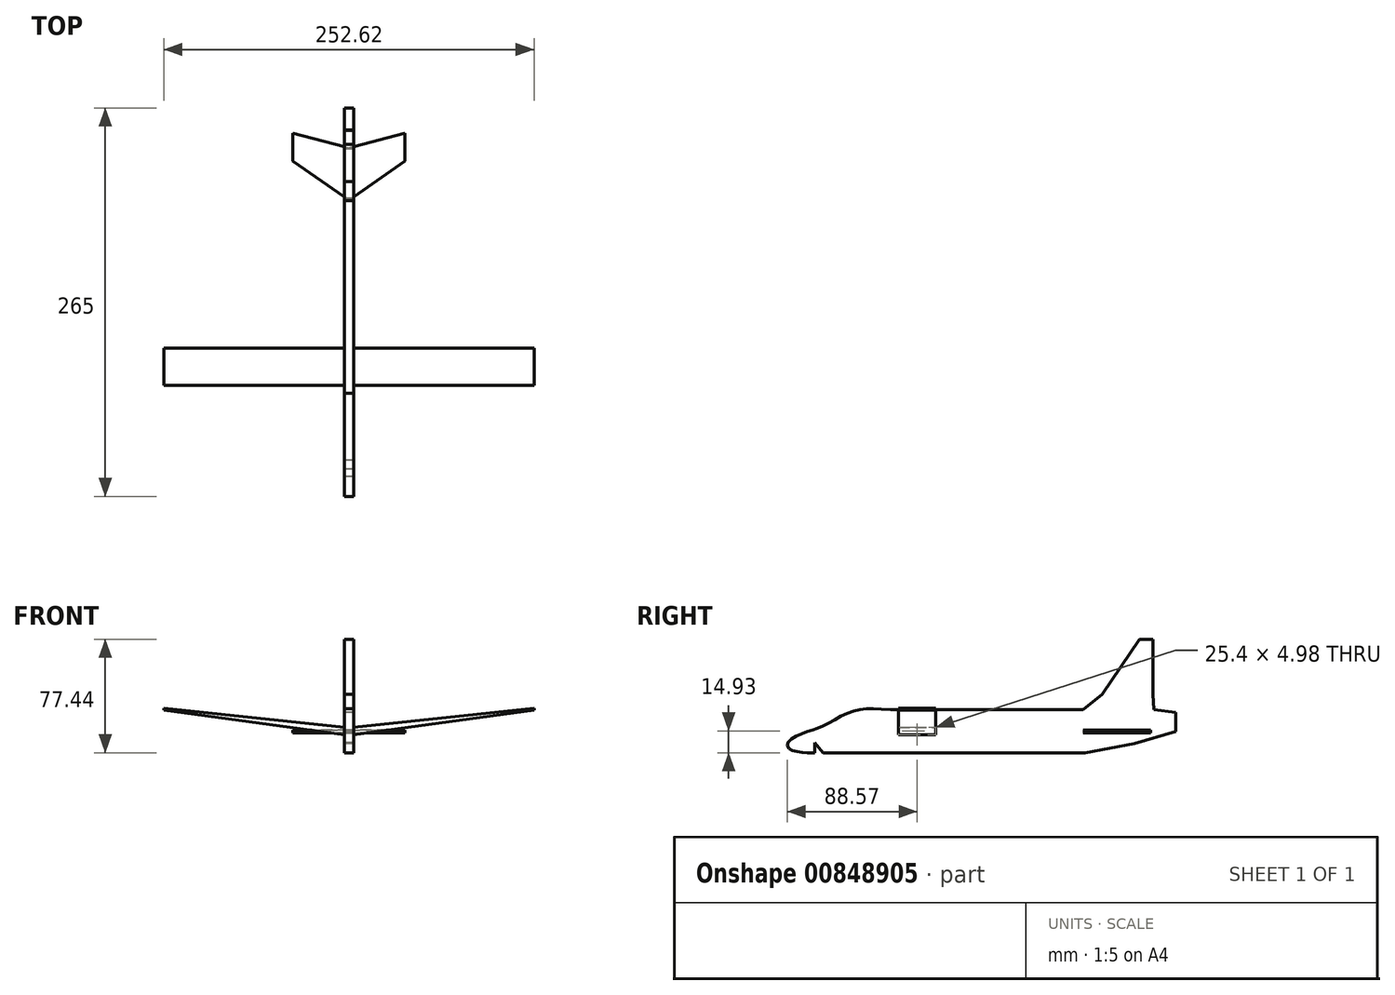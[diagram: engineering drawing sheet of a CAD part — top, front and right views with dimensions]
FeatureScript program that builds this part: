
annotation { "Feature Type Name" : "Feature", "Feature Type Description" : "" }
export const myFeature = defineFeature(function(context is Context, id is Id, definition is map)
    precondition{}
    {
        {
            var Q0;
            Q0=qCreatedBy(makeId("Right.planeOp"),FACE);
            var sketch = newSketch(context, id + "F0", { "sketchPlane" : qUnion([Q0])});
            skLineSegment(sketch, "E0", {"start": v(78.98, -14.55) * mm, "end": v(-51.3, -14.55) * mm});
            skFitSpline(sketch, "E1", {"points": [v(-62.34, -14.55) * mm, v(-73.33, -12.67) * mm, v(-75.7, -8.22) * mm, v(-65.02, -1.1) * mm, v(-51.06, 3.95) * mm, v(-30.97, 13.94) * mm, v(-5.48, 14.83) * mm], "startDerivative": vector(-70.22, 10.78) * mm, "endDerivative": vector(152.13, -6.73) * mm});
            skLineSegment(sketch, "E2", {"start": v(-5.48, 14.83) * mm, "end": v(76.3, 14.83) * mm});
            skLineSegment(sketch, "E3", {"start": v(76.3, 14.83) * mm, "end": v(126.07, 14.83) * mm});
            skLineSegment(sketch, "E4", {"start": v(126.07, 14.83) * mm, "end": v(138.96, 25.3) * mm});
            skLineSegment(sketch, "E5", {"start": v(138.96, 25.3) * mm, "end": v(164.55, 62.89) * mm});
            skLineSegment(sketch, "E6", {"start": v(164.55, 62.89) * mm, "end": v(173.84, 62.89) * mm});
            skLineSegment(sketch, "E7", {"start": v(173.84, 62.89) * mm, "end": v(173.84, 25.3) * mm});
            skLineSegment(sketch, "E8", {"start": v(173.84, 25.3) * mm, "end": v(174.18, 14.83) * mm});
            skPoint(sketch, "E9.startDerivative.orphan", {"position": v(194.66, 0) * mm});
            skLineSegment(sketch, "E10", {"start": v(174.18, 14.83) * mm, "end": v(189.13, 13) * mm});
            skLineSegment(sketch, "E11", {"start": v(189.13, 13) * mm, "end": v(189.13, -0.14) * mm});
            skLineSegment(sketch, "E12", {"start": v(189.13, -0.14) * mm, "end": v(161.15, -8.35) * mm});
            skLineSegment(sketch, "E13", {"start": v(161.15, -8.35) * mm, "end": v(127.42, -14.55) * mm});
            skLineSegment(sketch, "E14", {"start": v(127.42, -14.55) * mm, "end": v(78.98, -14.55) * mm});
            skLineSegment(sketch, "E15", {"start": v(-51.3, -14.55) * mm, "end": v(-57.24, -7.52) * mm});
            skLineSegment(sketch, "E16", {"start": v(-57.24, -14.55) * mm, "end": v(-57.24, -7.52) * mm});
            skLineSegment(sketch, "E17.trimOffspring", {"start": v(-57.24, -14.55) * mm, "end": v(-62.34, -14.55) * mm});
            skSolve(sketch);
        }
        {
            var Q0;
            Q0=qCreatedBy(makeId("Top.planeOp"),FACE);
            var sketch = newSketch(context, id + "F1", { "sketchPlane" : qUnion([Q0])});
            skLineSegment(sketch, "E18", {"start": v(0, 126.19) * mm, "end": v(38.25, 152.85) * mm});
            skLineSegment(sketch, "E19", {"start": v(38.25, 152.85) * mm, "end": v(38.25, 171.97) * mm});
            skLineSegment(sketch, "E20", {"start": v(38.25, 171.97) * mm, "end": v(0, 161.9) * mm});
            skLineSegment(sketch, "E21.MirrorCS", {"start": v(-38.25, 171.97) * mm, "end": v(0, 161.9) * mm});
            skLineSegment(sketch, "E22.MirrorCS", {"start": v(-38.25, 152.85) * mm, "end": v(-38.25, 171.97) * mm});
            skLineSegment(sketch, "E23.MirrorCS", {"start": v(0, 126.19) * mm, "end": v(-38.25, 152.85) * mm});
            skSolve(sketch);
        }
        {
            var Q0;
            Q0 = qSketchRegion(id + "F1", true);
            extrude(context, id + "F2", {"entities" : qUnion([Q0]), "endBound" : BoundingType.SYMMETRIC, "depth" : 1.78 * mm, "offsetDistance" : 25.4 * mm});
        }
        {
            var Q0;
            Q0 = qSketchRegion(id + "F0", true);
            extrude(context, id + "F3", {"entities" : qUnion([Q0]), "endBound" : BoundingType.SYMMETRIC, "depth" : 6.35 * mm, "offsetDistance" : 25.4 * mm});
        }
        {
            var Q0;
            Q0=qCreatedBy(makeId("Front.planeOp"),FACE);
            var sketch = newSketch(context, id + "F4", { "sketchPlane" : qUnion([Q0])});
            skLineSegment(sketch, "E24.0", {"start": v(-126.31, 15.76) * mm, "end": v(-126.31, 14.49) * mm});
            skLineSegment(sketch, "E25", {"start": v(0, 2.54) * mm, "end": v(0, -2.54) * mm});
            skLineSegment(sketch, "E26", {"start": v(-126.31, 15.76) * mm, "end": v(0, 2.54) * mm});
            skLineSegment(sketch, "E27", {"start": v(-126.31, 14.49) * mm, "end": v(0, -2.54) * mm});
            skPoint(sketch, "E28", {"position": v(0, 0) * mm});
            skLineSegment(sketch, "E29", {"start": v(0, -2.54) * mm, "end": v(0, 2.54) * mm});
            skSolve(sketch);
        }
        {
            var Q0;
            {var subQ0=sQuery(id+"F4.wireOp",EDGE,"E26");Q0=makeQuery(id+"F4.imprint","IMPRINT",FACE,{"disambiguationData":[TD([[makeQuery(id+"F4.imprint","IMPRINT",EDGE,{"derivedFrom":subQ0}),-1.0]])]});}
            extrude(context, id + "F5", {"entities" : qUnion([Q0]), "operationType" : NewBodyOperationType.ADD, "oppositeDirection" : true, "depth" : 25.4 * mm, "offsetDistance" : 25.4 * mm});
        }
        {
            var Q0;
            Q0=makeQuery(id+"F3.opExtrude","SWEPT_BODY",BODY,{"disambiguationData":[OSD([sQuery(id+"F0.wireOp",EDGE,"E0"),sQuery(id+"F0.wireOp",EDGE,"E1"),sQuery(id+"F0.wireOp",EDGE,"E2"),sQuery(id+"F0.wireOp",EDGE,"E3"),sQuery(id+"F0.wireOp",EDGE,"E4"),sQuery(id+"F0.wireOp",EDGE,"E5"),sQuery(id+"F0.wireOp",EDGE,"E6"),sQuery(id+"F0.wireOp",EDGE,"E7"),sQuery(id+"F0.wireOp",EDGE,"E8"),sQuery(id+"F0.wireOp",EDGE,"E10"),sQuery(id+"F0.wireOp",EDGE,"E11"),sQuery(id+"F0.wireOp",EDGE,"E12"),sQuery(id+"F0.wireOp",EDGE,"E13"),sQuery(id+"F0.wireOp",EDGE,"E14"),sQuery(id+"F0.wireOp",EDGE,"E15"),sQuery(id+"F0.wireOp",EDGE,"E16"),sQuery(id+"F0.wireOp",EDGE,"E17.trimOffspring")])]});
            var Q1;
            Q1=qCreatedBy(makeId("Right.planeOp"),FACE);
            mirror(context, id + "F6", {"entities" : qUnion([Q0]), "mirrorPlane" : qUnion([Q1])});
        }
    });
